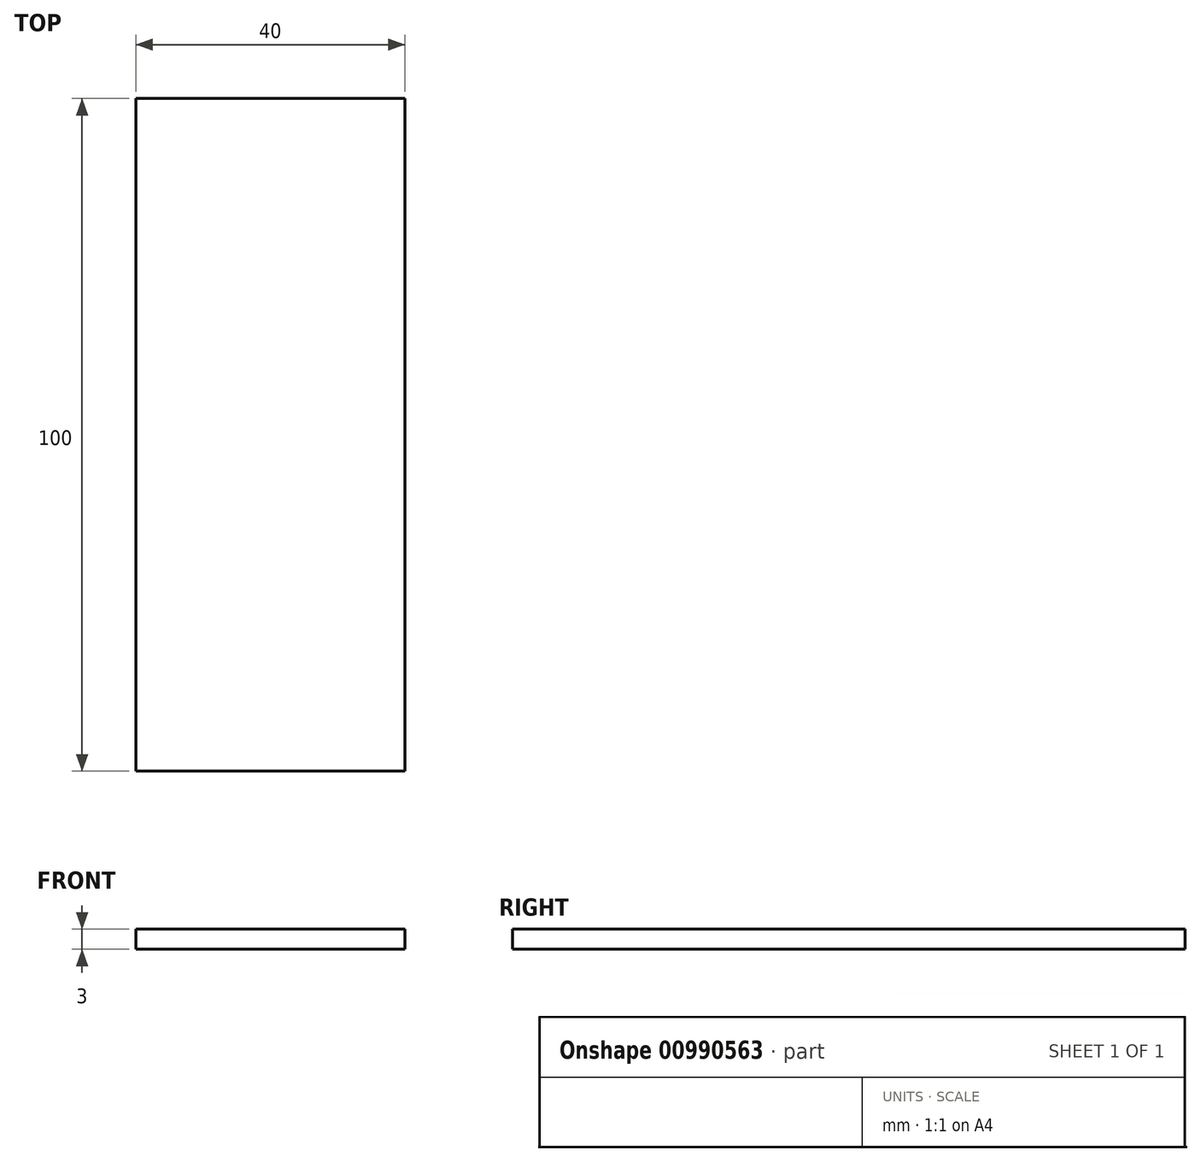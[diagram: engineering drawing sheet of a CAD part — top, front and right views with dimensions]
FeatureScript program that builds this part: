
annotation { "Feature Type Name" : "Feature", "Feature Type Description" : "" }
export const myFeature = defineFeature(function(context is Context, id is Id, definition is map)
    precondition{}
    {
        {
            var Q0;
            Q0=qCreatedBy(makeId("Top.planeOp"),FACE);
            var sketch = newSketch(context, id + "F0", { "sketchPlane" : qUnion([Q0])});
            skLineSegment(sketch, "E0.bottom", {"start": v(0, 0) * mm, "end": v(40, 0) * mm});
            skLineSegment(sketch, "E0.top", {"start": v(0, -100) * mm, "end": v(40, -100) * mm});
            skLineSegment(sketch, "E0.left", {"start": v(0, 0) * mm, "end": v(0, -100) * mm});
            skLineSegment(sketch, "E0.right", {"start": v(40, 0) * mm, "end": v(40, -100) * mm});
            skSolve(sketch);
        }
        {
            var Q0;
            Q0 = qSketchRegion(id + "F0", true);
            extrude(context, id + "F1", {"entities" : qUnion([Q0]), "oppositeDirection" : true, "depth" : 3 * mm, "offsetDistance" : 25 * mm});
        }
    });
